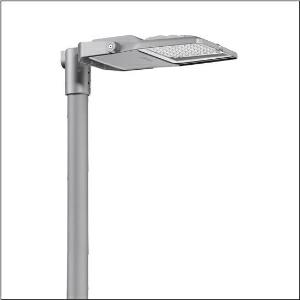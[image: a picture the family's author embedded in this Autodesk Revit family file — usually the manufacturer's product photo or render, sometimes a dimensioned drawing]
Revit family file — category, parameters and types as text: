
# Revit family: floodlight_fl_21_iq_mini___pl61_5xa7771b2c3a_a4a3
name_source: partatom
category: Lighting Fixtures
units: mm (PartAtom-declared; Revit-internal decimal feet)

## family parameters
Cut with Voids When Loaded = No
Host = Face
Light Source = No
Part Type = Normal
Room Calculation Point = No
Round Connector Dimension = Use Diameter
Shared = No

## types (1)
- --- (1 x LED, 6120 lm, 45.5 W, 3000K)
    Apparent Load = 46 VA
    CIE Flux Codes = 33 65 98 100 100
    Color Rendering = 70
    Color Temperature = 3000K
    Default Elevation = 1800 mm
    Description = Floodlight FL 21 iQ mini, floodlight, primary light control with lens, of PMMA, primary optical cover: protective disc, of toughened safety glass, transparent, light distribution: PL61, light emission: direct distribution, installation type: surface-mounted, LED, High Power LED, rated luminous flux: 6.120lm, luminous efficacy: 135lm/W, light colour: 730, colour temperature: 3000K, control: Auto-Match, Temp-Guard, Lumen-Switch, Night-Set, Smart-Wire, Light-Fading, Desk-Remote (wireless, voltage-free reading and setting of iQ features in the workshop via application-optimized NFC function/RFID function), optimised constant luminous flux control (CLO 2.0), with terminal, 6-pole, mains connection: 220..240V, AC, 50/60Hz, start of lifetime: 46W, end of service life: 48W, reduction: 22W, luminaire housing, of diecast aluminium, powder-coated, Siteco® metallic grey (DB 702S), corrosivity category C5 mid according to DIN EN ISO 12944, sealing non-destructively replaceable, please order mast flange separately, mast bracket, of steel, galvanised, powder-coated, Siteco® metallic grey (DB 702S), protection rating (complete): IP66, insulation class (complete): insulation class II (safety insulation), certification: CE, ENEC, VDE, protection symbol: D, impact resistance: IK08, permissible operating ambient temperature: -40..+40°C, permissible operating ambient temperature for outdoor applications: -40..+50°C, standard: DIN EN 12944, LABS conformity tested according to VDMA 24364:2018-05, packaging unit: 1 piece

Light Distribution: PL61
    Height = 70 mm
    Lamp = 1 x LED
    Lamp Light Flux = 6120 lm
    Lamp Power = 45.5 W
    Lamp count = 1
    Length = 485 mm
    Luminous efficacy = 135 lm/W
    Manufacturer = Siteco
    ModVariant = No
    Model = 5XA7771B2C3A
    Number of Poles = 1
    OnlyDefault = Yes
    Power Factor = 1
    Product Name = Floodlight FL 21 iQ mini | PL61
    Product group = floodlight | pylon annexe
    ProductGroupID = 6200
    Protection Class = Protection class II
    Protection Degree = IP 66
    RLX_Detail_Level = 1
    RLX_Emergency_Light_Flux = 0 lm
    RLX_Emergency_Type = 0
    RLX_Emergency_Type_DB = No
    RlxData = <blob elided: 101245 chars, md5=a41d6eac>
    Socket = socket
    Standby Power = 0 W
    System Light Flux = 6120 lm
    System Power = 46 W
    Type Comments = factory setting: luminous flux: 100 % | dim-lin: 254 | 463 mA
    Type Image = l_1007125.jpg
    URL = http://relux.com
    VarID = @adj_144945
    Voltage = 0 V
    Weight = 0.00 kg
    Width = 337 mm

## geometry (parser evidence)
native form markers: Blend x4, Sweep x11
no freeform markers — native parametric forms only
